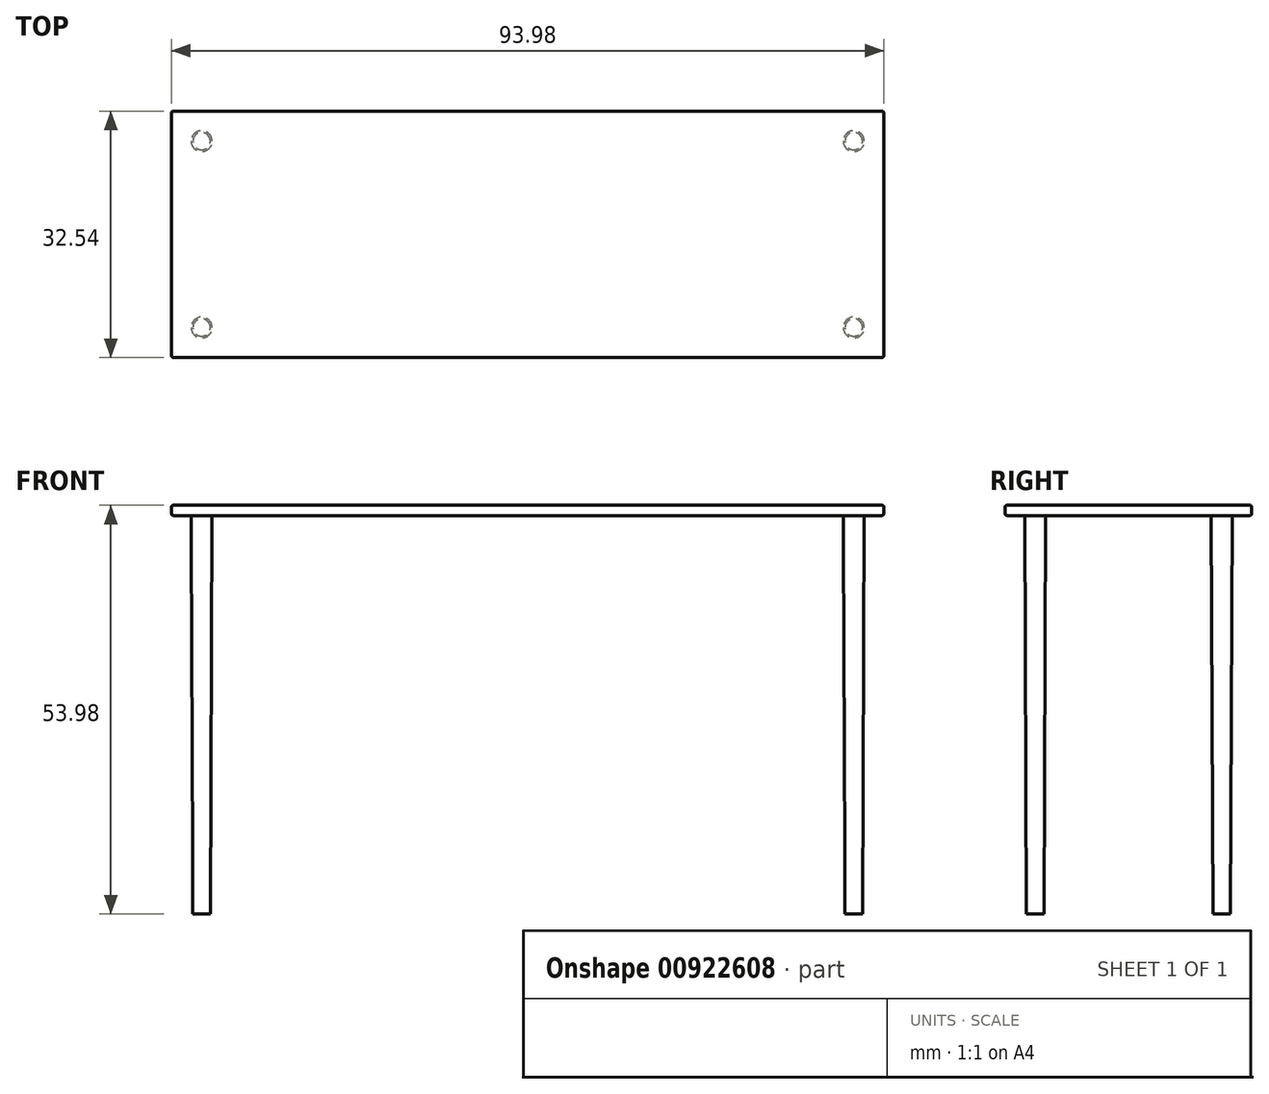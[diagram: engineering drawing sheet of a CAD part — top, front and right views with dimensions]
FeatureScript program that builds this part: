
annotation { "Feature Type Name" : "Feature", "Feature Type Description" : "" }
export const myFeature = defineFeature(function(context is Context, id is Id, definition is map)
    precondition{}
    {
        {
            var Q0;
            Q0=qCreatedBy(makeId("Top.planeOp"),FACE);
            var sketch = newSketch(context, id + "F0", { "sketchPlane" : qUnion([Q0])});
            skLineSegment(sketch, "E0.bottom", {"start": v(939.8, 325.44) * mm, "end": v(-939.8, 325.44) * mm});
            skLineSegment(sketch, "E0.top", {"start": v(939.8, -325.44) * mm, "end": v(-939.8, -325.44) * mm});
            skLineSegment(sketch, "E0.left", {"start": v(939.8, 325.44) * mm, "end": v(939.8, -325.44) * mm});
            skLineSegment(sketch, "E0.right", {"start": v(-939.8, 325.44) * mm, "end": v(-939.8, -325.44) * mm});
            skPoint(sketch, "E0.middle", {"position": v(0, 0) * mm});
            skSolve(sketch);
        }
        {
            var Q0;
            Q0 = qSketchRegion(id + "F0", true);
            extrude(context, id + "F1", {"entities" : qUnion([Q0]), "depth" : 26.99 * mm, "offsetDistance" : 25.4 * mm});
        }
        {
            var Q0;
            Q0=makeQuery(id+"F1.opExtrude","SWEPT_EDGE",EDGE,{"disambiguationData":[OSD([sQuery(id+"F0.wireOp",EDGE,"E0.bottom"),sQuery(id+"F0.wireOp",EDGE,"E0.right")])]});
            var Q1;
            Q1=makeQuery(id+"F1.opExtrude","SWEPT_FACE",FACE,{"disambiguationData":[OSD([sQuery(id+"F0.wireOp",EDGE,"E0.top")])]});
            var Q2;
            Q2=makeQuery(id+"F1.opExtrude","SWEPT_FACE",FACE,{"disambiguationData":[OSD([sQuery(id+"F0.wireOp",EDGE,"E0.right")])]});
            var Q3;
            Q3=makeQuery(id+"F1.opExtrude","CAP_EDGE",EDGE,{"disambiguationData":[OSD([sQuery(id+"F0.wireOp",EDGE,"E0.top")])],"isStart":false});
            var Q4;
            Q4=makeQuery(id+"F1.opExtrude","CAP_EDGE",EDGE,{"disambiguationData":[OSD([sQuery(id+"F0.wireOp",EDGE,"E0.right")])],"isStart":false});
            var Q5;
            Q5=makeQuery(id+"F1.opExtrude","SWEPT_EDGE",EDGE,{"disambiguationData":[OSD([sQuery(id+"F0.wireOp",EDGE,"E0.top"),sQuery(id+"F0.wireOp",EDGE,"E0.left")])]});
            var Q6;
            Q6=makeQuery(id+"F1.opExtrude","SWEPT_EDGE",EDGE,{"disambiguationData":[OSD([sQuery(id+"F0.wireOp",EDGE,"E0.top"),sQuery(id+"F0.wireOp",EDGE,"E0.right")])]});
            var Q7;
            Q7=makeQuery(id+"F1.opExtrude","CAP_EDGE",EDGE,{"disambiguationData":[OSD([sQuery(id+"F0.wireOp",EDGE,"E0.top")])],"isStart":true});
            var Q8;
            Q8=makeQuery(id+"F1.opExtrude","CAP_EDGE",EDGE,{"disambiguationData":[OSD([sQuery(id+"F0.wireOp",EDGE,"E0.right")])],"isStart":true});
            var Q9;
            Q9=makeQuery(id+"F1.opExtrude","SWEPT_FACE",FACE,{"disambiguationData":[OSD([sQuery(id+"F0.wireOp",EDGE,"E0.bottom")])]});
            var Q10;
            Q10=makeQuery(id+"F1.opExtrude","CAP_FACE",FACE,{"disambiguationData":[OSD([sQuery(id+"F0.wireOp",EDGE,"E0.bottom"),sQuery(id+"F0.wireOp",EDGE,"E0.top"),sQuery(id+"F0.wireOp",EDGE,"E0.left"),sQuery(id+"F0.wireOp",EDGE,"E0.right")])],"isStart":true});
            var Q11;
            Q11=makeQuery(id+"F1.opExtrude","CAP_FACE",FACE,{"disambiguationData":[OSD([sQuery(id+"F0.wireOp",EDGE,"E0.bottom"),sQuery(id+"F0.wireOp",EDGE,"E0.top"),sQuery(id+"F0.wireOp",EDGE,"E0.left"),sQuery(id+"F0.wireOp",EDGE,"E0.right")])],"isStart":false});
            var Q12;
            Q12=makeQuery(id+"F1.opExtrude","SWEPT_FACE",FACE,{"disambiguationData":[OSD([sQuery(id+"F0.wireOp",EDGE,"E0.left")])]});
            var Q13;
            Q13=makeQuery(id+"F1.opExtrude","CAP_EDGE",EDGE,{"disambiguationData":[OSD([sQuery(id+"F0.wireOp",EDGE,"E0.bottom")])],"isStart":false});
            var Q14;
            Q14=makeQuery(id+"F1.opExtrude","CAP_EDGE",EDGE,{"disambiguationData":[OSD([sQuery(id+"F0.wireOp",EDGE,"E0.left")])],"isStart":true});
            var Q15;
            Q15=makeQuery(id+"F1.opExtrude","SWEPT_EDGE",EDGE,{"disambiguationData":[OSD([sQuery(id+"F0.wireOp",EDGE,"E0.bottom"),sQuery(id+"F0.wireOp",EDGE,"E0.left")])]});
            var Q16;
            Q16=makeQuery(id+"F1.opExtrude","CAP_EDGE",EDGE,{"disambiguationData":[OSD([sQuery(id+"F0.wireOp",EDGE,"E0.bottom")])],"isStart":true});
            var Q17;
            Q17=makeQuery(id+"F1.opExtrude","CAP_EDGE",EDGE,{"disambiguationData":[OSD([sQuery(id+"F0.wireOp",EDGE,"E0.left")])],"isStart":false});
            fillet(context, id + "F2", {"entities" : qUnion([Q0, Q1, Q2, Q3, Q4, Q5, Q6, Q7, Q8, Q9, Q10, Q11, Q12, Q13, Q14, Q15, Q16, Q17]), "radius" : 5.08 * mm, "tangentPropagation" : true, "allowEdgeOverflow" : false});
        }
        {
            var Q0;
            Q0=makeQuery(id+"F1.opExtrude","CAP_FACE",FACE,{"disambiguationData":[OSD([sQuery(id+"F0.wireOp",EDGE,"E0.bottom"),sQuery(id+"F0.wireOp",EDGE,"E0.top"),sQuery(id+"F0.wireOp",EDGE,"E0.left"),sQuery(id+"F0.wireOp",EDGE,"E0.right")])],"isStart":true});
            var sketch = newSketch(context, id + "F3", { "sketchPlane" : qUnion([Q0])});
            skCircle(sketch, "E1", {"center": v(-860.43, 246.06) * mm, "radius": 27.56 * mm});
            skCircle(sketch, "E2", {"center": v(-860.43, -246.06) * mm, "radius": 27.56 * mm});
            skCircle(sketch, "E3", {"center": v(860.42, 246.06) * mm, "radius": 27.56 * mm});
            skCircle(sketch, "E4", {"center": v(860.42, -246.06) * mm, "radius": 27.56 * mm});
            skLineSegment(sketch, "E5", {"start": v(-860.43, 246.06) * mm, "end": v(860.42, 246.06) * mm, "construction": true});
            skLineSegment(sketch, "E6", {"start": v(-860.43, 246.06) * mm, "end": v(-860.43, -246.06) * mm, "construction": true});
            skLineSegment(sketch, "E7", {"start": v(860.42, -246.06) * mm, "end": v(860.42, 246.06) * mm, "construction": true});
            skLineSegment(sketch, "E8", {"start": v(-860.43, -246.06) * mm, "end": v(860.42, -246.06) * mm, "construction": true});
            skSolve(sketch);
        }
        {
            var Q0;
            Q0 = qSketchRegion(id + "F3", true);
            extrude(context, id + "F4", {"entities" : qUnion([Q0]), "operationType" : NewBodyOperationType.ADD, "depth" : 1052.5 * mm, "offsetDistance" : 25.4 * mm, "hasDraft" : true, "draftAngle" : 0.25 * degree, "draftPullDirection" : true});
        }
        {
            var Q0;
            Q0=makeQuery(id+"F1.opExtrude","SWEPT_BODY",BODY,{"disambiguationData":[OSD([sQuery(id+"F0.wireOp",EDGE,"E0.bottom"),sQuery(id+"F0.wireOp",EDGE,"E0.top"),sQuery(id+"F0.wireOp",EDGE,"E0.left"),sQuery(id+"F0.wireOp",EDGE,"E0.right")])]});
            var Q1;
            Q1=qCreatedBy(makeId("Origin.pointOp"),VERTEX);
            transform(context, id + "F5", {"entities" : qUnion([Q0]), "transformType" : TransformType.SCALE_UNIFORMLY, "scale" : 0.05, "scalePoint" : qUnion([Q1]), "makeCopy" : false});
        }
    });
